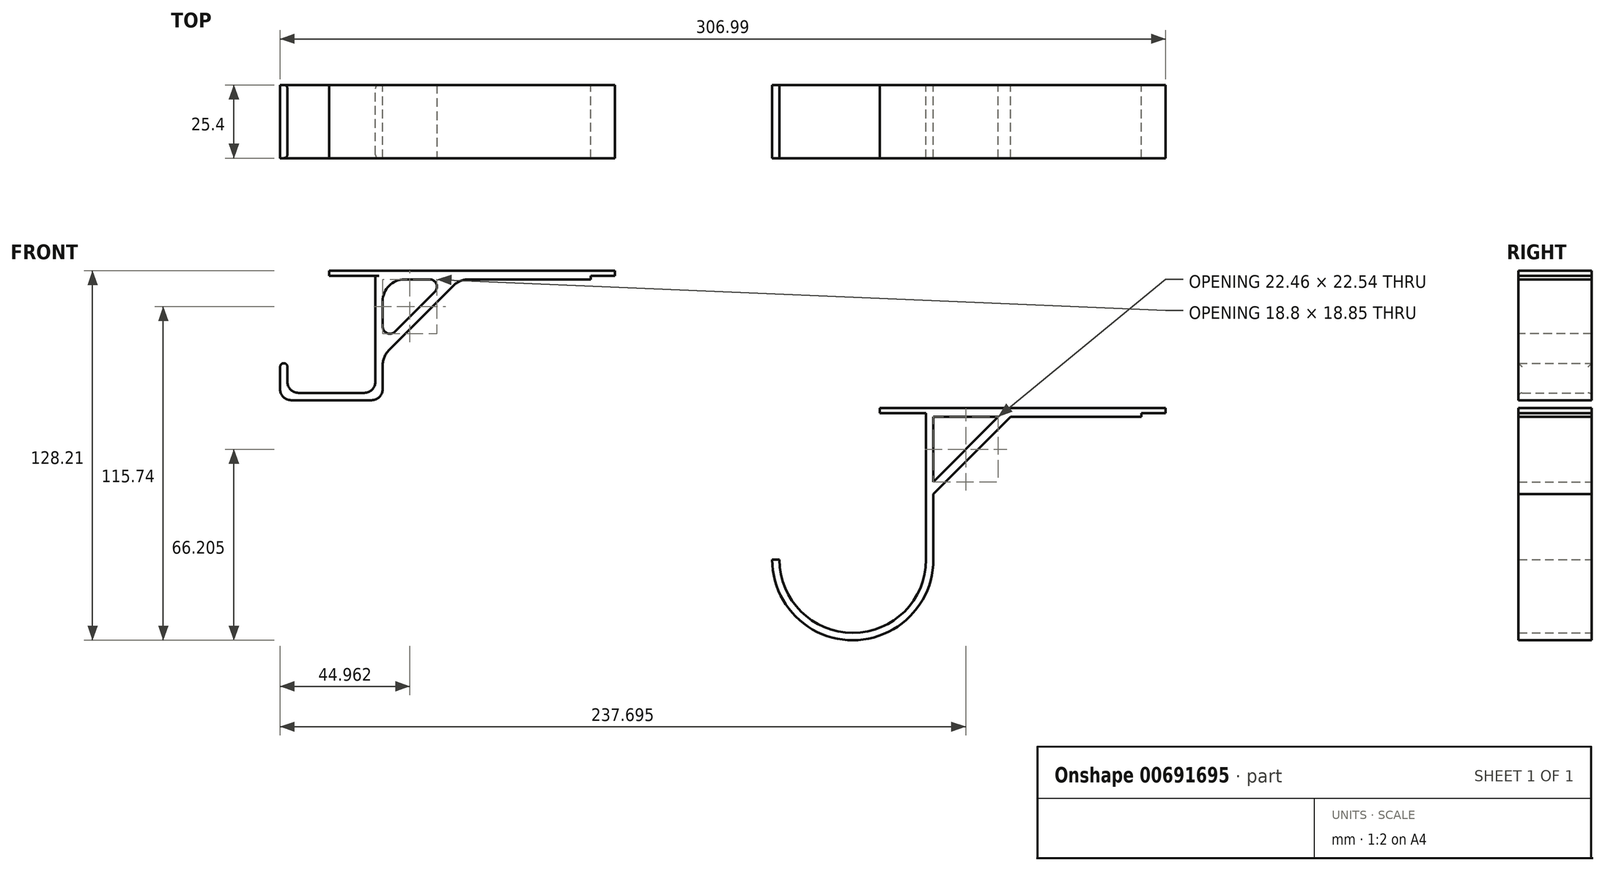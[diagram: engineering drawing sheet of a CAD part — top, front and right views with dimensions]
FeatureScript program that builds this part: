
annotation { "Feature Type Name" : "Feature", "Feature Type Description" : "" }
export const myFeature = defineFeature(function(context is Context, id is Id, definition is map)
    precondition{}
    {
        {
            var Q0;
            Q0=qCreatedBy(makeId("Front.planeOp"),FACE);
            var sketch = newSketch(context, id + "F0", { "sketchPlane" : qUnion([Q0])});
            skLineSegment(sketch, "E0", {"start": v(-45.25, 65.11) * mm, "end": v(53.8, 65.11) * mm});
            skLineSegment(sketch, "E1", {"start": v(53.8, 65.11) * mm, "end": v(53.8, 63.34) * mm});
            skLineSegment(sketch, "E2", {"start": v(53.8, 63.34) * mm, "end": v(45.43, 63.34) * mm});
            skLineSegment(sketch, "E3", {"start": v(45.43, 63.34) * mm, "end": v(45.43, 62.07) * mm});
            skLineSegment(sketch, "E4", {"start": v(-29.25, 63.34) * mm, "end": v(-45.25, 63.34) * mm});
            skLineSegment(sketch, "E5", {"start": v(-45.25, 63.34) * mm, "end": v(-45.25, 65.11) * mm});
            skLineSegment(sketch, "E6", {"start": v(-29.25, 22.7) * mm, "end": v(-59.73, 22.7) * mm});
            skLineSegment(sketch, "E7", {"start": v(-59.73, 22.7) * mm, "end": v(-59.73, 32.97) * mm});
            skLineSegment(sketch, "E8", {"start": v(-59.73, 32.97) * mm, "end": v(-62.27, 32.97) * mm});
            skLineSegment(sketch, "E9", {"start": v(-62.27, 32.97) * mm, "end": v(-62.27, 20.16) * mm});
            skLineSegment(sketch, "E10", {"start": v(-29.25, 63.34) * mm, "end": v(-29.25, 22.7) * mm});
            skLineSegment(sketch, "E11", {"start": v(-62.27, 20.16) * mm, "end": v(-26.7, 20.16) * mm});
            skLineSegment(sketch, "E12", {"start": v(45.43, 62.07) * mm, "end": v(0, 62.07) * mm});
            skLineSegment(sketch, "E13", {"start": v(-26.7, 35.36) * mm, "end": v(-26.7, 20.16) * mm});
            skLineSegment(sketch, "E14", {"start": v(-26.7, 35.36) * mm, "end": v(0, 62.07) * mm});
            skLineSegment(sketch, "E15", {"start": v(-26.7, 39.6) * mm, "end": v(-26.7, 62.07) * mm});
            skLineSegment(sketch, "E16", {"start": v(-26.7, 62.07) * mm, "end": v(-4.32, 62.07) * mm});
            skLineSegment(sketch, "E17", {"start": v(-4.32, 62.07) * mm, "end": v(-26.7, 39.6) * mm});
            skSolve(sketch);
        }
        {
            var Q0;
            Q0 = qSketchRegion(id + "F0", true);
            extrude(context, id + "F1", {"entities" : qUnion([Q0]), "depth" : 25.4 * mm, "offsetDistance" : 25.4 * mm});
        }
        {
            var Q0;
            Q0=makeQuery(id+"F1.opExtrude","SWEPT_EDGE",EDGE,{"disambiguationData":[OSD([sQuery(id+"F0.wireOp",EDGE,"E13"),sQuery(id+"F0.wireOp",EDGE,"E14")])]});
            var Q1;
            Q1=makeQuery(id+"F1.opExtrude","SWEPT_EDGE",EDGE,{"disambiguationData":[OSD([sQuery(id+"F0.wireOp",EDGE,"E12"),sQuery(id+"F0.wireOp",EDGE,"E14")])]});
            var Q2;
            Q2=makeQuery(id+"F1.opExtrude","SWEPT_EDGE",EDGE,{"disambiguationData":[OSD([sQuery(id+"F0.wireOp",EDGE,"E15"),sQuery(id+"F0.wireOp",EDGE,"E16")])]});
            fillet(context, id + "F2", {"entities" : qUnion([Q0, Q1, Q2]), "radius" : 7.62 * mm, "tangentPropagation" : true, "allowEdgeOverflow" : false});
        }
        {
            var Q0;
            Q0=makeQuery(id+"F1.opExtrude","SWEPT_EDGE",EDGE,{"disambiguationData":[OSD([sQuery(id+"F0.wireOp",EDGE,"E15"),sQuery(id+"F0.wireOp",EDGE,"E17")])]});
            var Q1;
            Q1=makeQuery(id+"F1.opExtrude","SWEPT_EDGE",EDGE,{"disambiguationData":[OSD([sQuery(id+"F0.wireOp",EDGE,"E16"),sQuery(id+"F0.wireOp",EDGE,"E17")])]});
            fillet(context, id + "F3", {"entities" : qUnion([Q0, Q1]), "radius" : 2.54 * mm, "tangentPropagation" : true, "allowEdgeOverflow" : false});
        }
        {
            var Q0;
            Q0=makeQuery(id+"F1.opExtrude","SWEPT_EDGE",EDGE,{"disambiguationData":[OSD([sQuery(id+"F0.wireOp",EDGE,"E6"),sQuery(id+"F0.wireOp",EDGE,"E10")])]});
            var Q1;
            Q1=makeQuery(id+"F1.opExtrude","SWEPT_EDGE",EDGE,{"disambiguationData":[OSD([sQuery(id+"F0.wireOp",EDGE,"E6"),sQuery(id+"F0.wireOp",EDGE,"E7")])]});
            var Q2;
            Q2=makeQuery(id+"F1.opExtrude","SWEPT_EDGE",EDGE,{"disambiguationData":[OSD([sQuery(id+"F0.wireOp",EDGE,"E11"),sQuery(id+"F0.wireOp",EDGE,"E13")])]});
            var Q3;
            Q3=makeQuery(id+"F1.opExtrude","SWEPT_EDGE",EDGE,{"disambiguationData":[OSD([sQuery(id+"F0.wireOp",EDGE,"E9"),sQuery(id+"F0.wireOp",EDGE,"E11")])]});
            fillet(context, id + "F4", {"entities" : qUnion([Q0, Q1, Q2, Q3]), "radius" : 3.8 * mm, "tangentPropagation" : true, "allowEdgeOverflow" : false});
        }
        {
            var Q0;
            Q0=makeQuery(id+"F1.opExtrude","CAP_EDGE",EDGE,{"disambiguationData":[OSD([sQuery(id+"F0.wireOp",EDGE,"E6")])],"isStart":false});
            var Q1;
            {var subQ0=sQuery(id+"F0.wireOp",EDGE,"E10");var subQ1=sQuery(id+"F0.wireOp",EDGE,"E6");Q1=makeQuery(id+"F4.opFillet","BLEND_EDGE",EDGE,{"blendedFrom":[makeQuery(id+"F1.opExtrude","SWEPT_EDGE",EDGE,{"disambiguationData":[OSD([subQ1,subQ0])]}),makeQuery(id+"F1.opExtrude","CAP_FACE",FACE,{"disambiguationData":[OSD([sQuery(id+"F0.wireOp",EDGE,"E0"),sQuery(id+"F0.wireOp",EDGE,"E1"),sQuery(id+"F0.wireOp",EDGE,"E2"),sQuery(id+"F0.wireOp",EDGE,"E3"),sQuery(id+"F0.wireOp",EDGE,"E4"),sQuery(id+"F0.wireOp",EDGE,"E5"),subQ1,sQuery(id+"F0.wireOp",EDGE,"E7"),sQuery(id+"F0.wireOp",EDGE,"E8"),sQuery(id+"F0.wireOp",EDGE,"E9"),subQ0,sQuery(id+"F0.wireOp",EDGE,"E11"),sQuery(id+"F0.wireOp",EDGE,"E12"),sQuery(id+"F0.wireOp",EDGE,"E13"),sQuery(id+"F0.wireOp",EDGE,"E14"),sQuery(id+"F0.wireOp",EDGE,"E15"),sQuery(id+"F0.wireOp",EDGE,"E16"),sQuery(id+"F0.wireOp",EDGE,"E17")])],"isStart":false})],"blendedInto":[makeQuery(id+"F1.opExtrude","CAP_FACE",FACE,{"disambiguationData":[OSD([sQuery(id+"F0.wireOp",EDGE,"E0"),sQuery(id+"F0.wireOp",EDGE,"E1"),sQuery(id+"F0.wireOp",EDGE,"E2"),sQuery(id+"F0.wireOp",EDGE,"E3"),sQuery(id+"F0.wireOp",EDGE,"E4"),sQuery(id+"F0.wireOp",EDGE,"E5"),subQ1,sQuery(id+"F0.wireOp",EDGE,"E7"),sQuery(id+"F0.wireOp",EDGE,"E8"),sQuery(id+"F0.wireOp",EDGE,"E9"),subQ0,sQuery(id+"F0.wireOp",EDGE,"E11"),sQuery(id+"F0.wireOp",EDGE,"E12"),sQuery(id+"F0.wireOp",EDGE,"E13"),sQuery(id+"F0.wireOp",EDGE,"E14"),sQuery(id+"F0.wireOp",EDGE,"E15"),sQuery(id+"F0.wireOp",EDGE,"E16"),sQuery(id+"F0.wireOp",EDGE,"E17")])],"isStart":false})]});}
            var Q2;
            Q2=makeQuery(id+"F1.opExtrude","CAP_EDGE",EDGE,{"disambiguationData":[OSD([sQuery(id+"F0.wireOp",EDGE,"E10")])],"isStart":false});
            var Q3;
            Q3=makeQuery(id+"F1.opExtrude","CAP_EDGE",EDGE,{"disambiguationData":[OSD([sQuery(id+"F0.wireOp",EDGE,"E10")])],"isStart":true});
            var Q4;
            {var subQ0=sQuery(id+"F0.wireOp",EDGE,"E10");var subQ1=sQuery(id+"F0.wireOp",EDGE,"E6");Q4=makeQuery(id+"F4.opFillet","BLEND_EDGE",EDGE,{"blendedFrom":[makeQuery(id+"F1.opExtrude","SWEPT_EDGE",EDGE,{"disambiguationData":[OSD([subQ1,subQ0])]}),makeQuery(id+"F1.opExtrude","CAP_FACE",FACE,{"disambiguationData":[OSD([sQuery(id+"F0.wireOp",EDGE,"E0"),sQuery(id+"F0.wireOp",EDGE,"E1"),sQuery(id+"F0.wireOp",EDGE,"E2"),sQuery(id+"F0.wireOp",EDGE,"E3"),sQuery(id+"F0.wireOp",EDGE,"E4"),sQuery(id+"F0.wireOp",EDGE,"E5"),subQ1,sQuery(id+"F0.wireOp",EDGE,"E7"),sQuery(id+"F0.wireOp",EDGE,"E8"),sQuery(id+"F0.wireOp",EDGE,"E9"),subQ0,sQuery(id+"F0.wireOp",EDGE,"E11"),sQuery(id+"F0.wireOp",EDGE,"E12"),sQuery(id+"F0.wireOp",EDGE,"E13"),sQuery(id+"F0.wireOp",EDGE,"E14"),sQuery(id+"F0.wireOp",EDGE,"E15"),sQuery(id+"F0.wireOp",EDGE,"E16"),sQuery(id+"F0.wireOp",EDGE,"E17")])],"isStart":true})],"blendedInto":[makeQuery(id+"F1.opExtrude","CAP_FACE",FACE,{"disambiguationData":[OSD([sQuery(id+"F0.wireOp",EDGE,"E0"),sQuery(id+"F0.wireOp",EDGE,"E1"),sQuery(id+"F0.wireOp",EDGE,"E2"),sQuery(id+"F0.wireOp",EDGE,"E3"),sQuery(id+"F0.wireOp",EDGE,"E4"),sQuery(id+"F0.wireOp",EDGE,"E5"),subQ1,sQuery(id+"F0.wireOp",EDGE,"E7"),sQuery(id+"F0.wireOp",EDGE,"E8"),sQuery(id+"F0.wireOp",EDGE,"E9"),subQ0,sQuery(id+"F0.wireOp",EDGE,"E11"),sQuery(id+"F0.wireOp",EDGE,"E12"),sQuery(id+"F0.wireOp",EDGE,"E13"),sQuery(id+"F0.wireOp",EDGE,"E14"),sQuery(id+"F0.wireOp",EDGE,"E15"),sQuery(id+"F0.wireOp",EDGE,"E16"),sQuery(id+"F0.wireOp",EDGE,"E17")])],"isStart":true})]});}
            var Q5;
            Q5=makeQuery(id+"F1.opExtrude","SWEPT_EDGE",EDGE,{"disambiguationData":[OSD([sQuery(id+"F0.wireOp",EDGE,"E7"),sQuery(id+"F0.wireOp",EDGE,"E8")])]});
            var Q6;
            Q6=makeQuery(id+"F1.opExtrude","SWEPT_EDGE",EDGE,{"disambiguationData":[OSD([sQuery(id+"F0.wireOp",EDGE,"E8"),sQuery(id+"F0.wireOp",EDGE,"E9")])]});
            fillet(context, id + "F5", {"entities" : qUnion([Q0, Q1, Q2, Q3, Q4, Q5, Q6]), "radius" : 1.27 * mm, "tangentPropagation" : true, "allowEdgeOverflow" : false});
        }
        {
            var Q0;
            Q0=qCreatedBy(makeId("Front.planeOp"),FACE);
            var sketch = newSketch(context, id + "F6", { "sketchPlane" : qUnion([Q0])});
            skLineSegment(sketch, "E18", {"start": v(-28.33, 17.42) * mm, "end": v(70.73, 17.42) * mm});
            skLineSegment(sketch, "E19", {"start": v(70.73, 17.42) * mm, "end": v(70.73, 15.64) * mm});
            skLineSegment(sketch, "E20", {"start": v(70.73, 15.64) * mm, "end": v(62.34, 15.64) * mm});
            skLineSegment(sketch, "E21", {"start": v(62.34, 15.64) * mm, "end": v(62.34, 14.37) * mm});
            skLineSegment(sketch, "E22", {"start": v(-12.33, 15.64) * mm, "end": v(-28.33, 15.64) * mm});
            skLineSegment(sketch, "E23", {"start": v(-28.33, 15.64) * mm, "end": v(-28.33, 17.42) * mm});
            skLineSegment(sketch, "E24", {"start": v(-12.33, 15.64) * mm, "end": v(-12.33, -35.16) * mm});
            skLineSegment(sketch, "E25", {"start": v(62.34, 14.37) * mm, "end": v(16.98, 14.37) * mm});
            skLineSegment(sketch, "E26", {"start": v(-9.8, -12.4) * mm, "end": v(-9.8, -35.08) * mm});
            skLineSegment(sketch, "E27", {"start": v(-9.8, -12.4) * mm, "end": v(16.98, 14.37) * mm});
            skLineSegment(sketch, "E28", {"start": v(-9.8, -8.16) * mm, "end": v(-9.8, 14.37) * mm});
            skLineSegment(sketch, "E29", {"start": v(-9.8, 14.37) * mm, "end": v(12.66, 14.37) * mm});
            skLineSegment(sketch, "E30", {"start": v(12.66, 14.37) * mm, "end": v(-9.8, -8.16) * mm});
            skArc(sketch, "E31", {"start": v(-63.13, -35.16) * mm, "mid": v(-37.73, -60.56) * mm, "end": v(-12.33, -35.16) * mm});
            skArc(sketch, "E32", {"start": v(-9.8, -35.08) * mm, "mid": v(-37.7, -63.1) * mm, "end": v(-65.67, -35.16) * mm});
            skLineSegment(sketch, "E33", {"start": v(-65.67, -35.16) * mm, "end": v(-63.13, -35.16) * mm});
            skSolve(sketch);
        }
        {
            var Q0;
            Q0 = qSketchRegion(id + "F6", true);
            extrude(context, id + "F7", {"entities" : qUnion([Q0]), "depth" : 25.4 * mm, "offsetDistance" : 25.4 * mm});
        }
        {
            var Q0;
            Q0=makeQuery(id+"F7.opExtrude","SWEPT_BODY",BODY,{"disambiguationData":[OSD([sQuery(id+"F6.wireOp",EDGE,"E18"),sQuery(id+"F6.wireOp",EDGE,"E19"),sQuery(id+"F6.wireOp",EDGE,"E20"),sQuery(id+"F6.wireOp",EDGE,"E21"),sQuery(id+"F6.wireOp",EDGE,"E22"),sQuery(id+"F6.wireOp",EDGE,"E23"),sQuery(id+"F6.wireOp",EDGE,"E24"),sQuery(id+"F6.wireOp",EDGE,"E25"),sQuery(id+"F6.wireOp",EDGE,"E26"),sQuery(id+"F6.wireOp",EDGE,"E27"),sQuery(id+"F6.wireOp",EDGE,"E28"),sQuery(id+"F6.wireOp",EDGE,"E29"),sQuery(id+"F6.wireOp",EDGE,"E30"),sQuery(id+"F6.wireOp",EDGE,"E31"),sQuery(id+"F6.wireOp",EDGE,"E32"),sQuery(id+"F6.wireOp",EDGE,"E33")])]});
            transform(context, id + "F8", {"entities" : qUnion([Q0]), "transformType" : TransformType.TRANSLATION_3D, "dx" : 174 * mm, "dy" : 0 * mm, "dz" : 0 * mm, "makeCopy" : false});
        }
    });
